# Revit family: O5DMH-NRG
name_source: partatom
category: Mechanical Equipment
revit_build: Autodesk Revit 2017 (Build: 20181011_1645(x64)
units: mm (PartAtom-declared; Revit-internal decimal feet)

## family parameters
Always vertical = Yes
Cut with Voids When Loaded = No
OmniClass Number = 23.40.40.11.17
OmniClass Title = Refrigerated Cases
Part Type = Normal
Room Calculation Point = No
Round Connector Dimension = Use Radius
Shared = No
Work Plane-Based = Yes

## types (36) — shared parameters
24" Shelf = Yes
BOTTOM ELECTRICAL = Yes
BOTTOM REFRIGERATION PIPING = Yes
Certifications = NSF 7, UL471, CSA
DATE = 05/02/2016
DRAIN PIPING = Yes
Default Elevation = 48"
Description = Multi-Deck Merchandiser
Discharge Air Velocity (FPM) = 150 FPM
EQUIPMENT DESCRIPTION = Multi-Deck Merchandiser
EQUIPMENT MARK = O5DMHQA-NRG
GLASS = Glass
Height = 85 5/8"
Item Description = Multi-Deck Merchandiser
LF STD END = Yes
Legend Number = O5DMHQA-NRG
Manufacturer = HILL PHOENIX
Model = O5DMHQA-NRG
PAINTED METAL UPPER SHELF = PAINTED SHELVES
REAR REFRIGERATION PIPING = Yes
REFRIGERATION PIPING = COPPER PIPE
RT STD END = Yes
STAINLESS STEEL = GALVANIZED STEEL
Standard Power Amps = 0 A
Superheat Set Point @ Bulb (°F) = 6-8 °F
TOP ELECTRICAL = Yes
TOP REFRIGERATION PIPING = Yes
Timed-Off Defrost Termination Temp = 42 °F
URL = http://www.hillphoenix.com
Width = 43 1/4"

## per-type parameters (varying)
| type | Application Discipline | BTUH Conventional | BTUH Parallel | CENTER LINE | DRAIN LINE | Defrosts Per Day | Discharge Air (°F) | Evaporator (°F) | High Efficiency Amps | High Efficiency Watts | High Power (Cornice) Amps | High Power (Cornice) Watts | Length | Length of Cases | Light Length | Lights Per Row | Number of Fans | Refgn | Standard Power Watts | Timed-Off Defrost Fail-Safe (Min) |
| 04' Dairy/Deli/Cut Produce with Std. Dairy Sill | Dairy/Deli/Cut Produce with 2.5 Extended Sill | 1531 | 1340 | 24" | 36" | 6 | 33 °F | 28 °F | 0 A | 18 W | 0 A | 22 W | 48" | 48" | 4' | 1 | 1 | 22 1/2" | 12 W | 40 (min) |
| 06' Dairy/Deli/Cut Produce with Std. Dairy Sill | Dairy/Deli/Cut Produce with Std. Dairy Sill | 1571 | 1375 | 36" | 36" | 6 | 33 °F | 28 °F | 0 A | 35 W | 0 A | 30 W | 72" | 72" | 3' | 2 | 2 | 28 5/8" | 17 W | 40 (min) |
| 08' Dairy/Deli/Cut Produce with Std. Dairy Sill | Dairy/Deli/Cut Produce with Std. Dairy Sill | 1571 | 1375 | 48" | 48" | 6 | 33 °F | 28 °F | 0 A | 35 W | 0 A | 43 W | 96" | 96" | 4' | 2 | 2 | 28 5/8" | 24 W | 40 (min) |
| 12' Dairy/Deli/Cut Produce with Std. Dairy Sill | Dairy/Deli/Cut Produce with Std. Dairy Sill | 1571 | 1375 | 72" | 72" | 6 | 33 °F | 28 °F | 1 A | 53 W | 1 A | 65 W | 144" | 144" | 4' | 3 | 3 | 28 5/8" | 36 W | 40 (min) |
| 04' Dairy/Deli/Cut Produce with 2.5 Extended Sill | Dairy/Deli/Cut Produce with 2.5 Extended Sill | 1531 | 1340 | 24" | 36" | 6 | 33 °F | 28 °F | 0 A | 18 W | 0 A | 22 W | 48" | 48" | 4' | 1 | 1 | 22 1/2" | 12 W | 40 (min) |
| 06' Dairy/Deli/Cut Produce with 2.5 Extended Sill | Dairy/Deli/Cut Produce with 2.5 Extended Sill | 1531 | 1340 | 36" | 36" | 6 | 33 °F | 28 °F | 0 A | 35 W | 0 A | 30 W | 72" | 72" | 3' | 2 | 2 | 28 5/8" | 17 W | 40 (min) |
| 08' Dairy/Deli/Cut Produce with 2.5 Extended Sill | Dairy/Deli/Cut Produce with 2.5 Extended Sill | 1531 | 1340 | 48" | 48" | 6 | 33 °F | 28 °F | 0 A | 35 W | 0 A | 43 W | 96" | 96" | 4' | 2 | 2 | 28 5/8" | 24 W | 40 (min) |
| 12' Dairy/Deli/Cut Produce with 2.5 Extended Sill | Dairy/Deli/Cut Produce with 2.5 Extended Sill | 1531 | 1340 | 72" | 72" | 6 | 33 °F | 28 °F | 1 A | 53 W | 1 A | 65 W | 144" | 144" | 4' | 3 | 3 | 28 5/8" | 36 W | 40 (min) |
| 04' Dairy/Deli/Cut Produce with 5 Extended Sill | Dairy/Deli/Cut Produce with 5 Extended Sill | 1503 | 1315 | 24" | 36" | 6 | 33 °F | 28 °F | 0 A | 18 W | 0 A | 22 W | 48" | 48" | 4' | 1 | 1 | 22 1/2" | 12 W | 40 (min) |
| 06' Dairy/Deli/Cut Produce with 5 Extended Sill | Dairy/Deli/Cut Produce with 5 Extended Sill | 1503 | 1315 | 36" | 36" | 6 | 33 °F | 28 °F | 0 A | 35 W | 0 A | 30 W | 72" | 72" | 3' | 2 | 2 | 28 5/8" | 17 W | 40 (min) |
| 08' Dairy/Deli/Cut Produce with 5 Extended Sill | Dairy/Deli/Cut Produce with 5 Extended Sill | 1503 | 1315 | 48" | 48" | 6 | 33 °F | 28 °F | 0 A | 35 W | 0 A | 43 W | 96" | 96" | 4' | 2 | 2 | 28 5/8" | 24 W | 40 (min) |
| 12' Dairy/Deli/Cut Produce with 5 Extended Sill | Dairy/Deli/Cut Produce with 5 Extended Sill | 1503 | 1315 | 72" | 72" | 6 | 33 °F | 28 °F | 1 A | 53 W | 1 A | 65 W | 144" | 144" | 4' | 3 | 3 | 28 5/8" | 36 W | 40 (min) |
| 04' Dairy/Deli/Cut Produce with 7.5 Extended Sill | Dairy/Deli/Cut Produce with 7.5 Extended Sill | 1480 | 1295 | 24" | 36" | 6 | 33 °F | 28 °F | 0 A | 18 W | 0 A | 22 W | 48" | 48" | 4' | 1 | 1 | 22 1/2" | 12 W | 40 (min) |
| 06' Dairy/Deli/Cut Produce with 7.5 Extended Sill | Dairy/Deli/Cut Produce with 7.5 Extended Sill | 1480 | 1295 | 36" | 36" | 6 | 33 °F | 28 °F | 0 A | 35 W | 0 A | 30 W | 72" | 72" | 3' | 2 | 2 | 28 5/8" | 17 W | 40 (min) |
| 08' Dairy/Deli/Cut Produce with 7.5 Extended Sill | Dairy/Deli/Cut Produce with 7.5 Extended Sill | 1480 | 1295 | 48" | 48" | 6 | 33 °F | 28 °F | 0 A | 35 W | 0 A | 43 W | 96" | 96" | 4' | 2 | 2 | 28 5/8" | 24 W | 40 (min) |
| 12' Dairy/Deli/Cut Produce with 7.5 Extended Sill | Dairy/Deli/Cut Produce with 7.5 Extended Sill | 1480 | 1295 | 72" | 72" | 6 | 33 °F | 28 °F | 1 A | 53 W | 1 A | 65 W | 144" | 144" | 4' | 3 | 3 | 28 5/8" | 36 W | 40 (min) |
| 04' Beverage Bulk Produce with 2.5 Extended Sill | Beverage/ Bulk Produce with 2.5 Extended Sill | 1291 | 1130 | 24" | 36" | 2 | 37 °F | 34 °F | 0 A | 18 W | 0 A | 22 W | 48" | 48" | 4' | 1 | 1 | 22 1/2" | 12 W | 30 (min) |
| 06' Beverage Bulk Produce with 2.5 Extended Sill | Beverage/ Bulk Produce with 2.5 Extended Sill | 1291 | 1130 | 36" | 36" | 2 | 37 °F | 34 °F | 0 A | 35 W | 0 A | 30 W | 72" | 72" | 3' | 2 | 2 | 28 5/8" | 17 W | 30 (min) |
| 08' Beverage Bulk Produce with 2.5 Extended Sill | Beverage/ Bulk Produce | 1291 | 1130 | 48" | 48" | 2 | 37 °F | 34 °F | 0 A | 35 W | 0 A | 43 W | 96" | 96" | 4' | 2 | 2 | 28 5/8" | 24 W | 30 (min) |
| 12' Beverage Bulk Produce with 2.5 Extended Sill | Beverage/ Bulk Produce with 2.5 Extended Sill | 1291 | 1130 | 72" | 72" | 2 | 37 °F | 34 °F | 1 A | 53 W | 1 A | 65 W | 144" | 144" | 4' | 3 | 3 | 28 5/8" | 36 W | 30 (min) |
| 04' Beverage Bulk Produce with 5 Extended Sill | Beverage/ Bulk Produce with 5 Extended Sill | 1263 | 1130 | 24" | 36" | 2 | 37 °F | 34 °F | 0 A | 18 W | 0 A | 22 W | 48" | 48" | 4' | 1 | 1 | 22 1/2" | 12 W | 30 (min) |
| 06' Beverage Bulk Produce with 5 Extended Sill | Beverage/ Bulk Produce | 1263 | 1105 | 36" | 36" | 2 | 37 °F | 34 °F | 0 A | 35 W | 0 A | 30 W | 72" | 72" | 3' | 2 | 2 | 28 5/8" | 17 W | 30 (min) |
| 08' Beverage Bulk Produce with 5 Extended Sill | Beverage/ Bulk Produce with 5 Extended Sill | 1263 | 1130 | 48" | 48" | 2 | 37 °F | 34 °F | 0 A | 35 W | 0 A | 43 W | 96" | 96" | 4' | 2 | 2 | 28 5/8" | 24 W | 30 (min) |
| 12' Beverage Bulk Produce with 5 Extended Sill | Beverage/ Bulk Produce with 5 Extended Sill | 1263 | 1105 | 72" | 72" | 2 | 37 °F | 34 °F | 1 A | 53 W | 1 A | 65 W | 144" | 144" | 4' | 3 | 3 | 28 5/8" | 36 W | 30 (min) |
| 04' Beverage Bulk Produce with 7.5 Extended Sill | Beverage/ Bulk Produce | 1240 | 1085 | 24" | 36" | 2 | 37 °F | 34 °F | 0 A | 18 W | 0 A | 22 W | 48" | 48" | 4' | 1 | 1 | 22 1/2" | 12 W | 30 (min) |
| 06' Beverage Bulk Produce with 7.5 Extended Sill | Beverage/ Bulk Produce with 7.5 Extended Sill | 1240 | 1085 | 36" | 36" | 2 | 37 °F | 34 °F | 0 A | 35 W | 0 A | 30 W | 72" | 72" | 3' | 2 | 2 | 28 5/8" | 17 W | 30 (min) |
| 08' Beverage Bulk Produce with 7.5 Extended Sill | Beverage/ Bulk Produce with 7.5 Extended Sill | 1240 | 1085 | 48" | 48" | 6 | 33 °F | 28 °F | 0 A | 35 W | 0 A | 43 W | 96" | 96" | 4' | 2 | 2 | 28 5/8" | 24 W | 40 (min) |
| 12' Beverage Bulk Produce with 7.5 Extended Sill | Beverage/ Bulk Produce with 7.5 Extended Sill | 1240 | 1085 | 72" | 72" | 2 | 37 °F | 34 °F | 1 A | 53 W | 1 A | 65 W | 144" | 144" | 4' | 3 | 3 | 28 5/8" | 36 W | 30 (min) |
| 04' Beverage Bulk Produce with Std. Dairy Sill | Beverage Bulk Produce with Std. Dairy Sill | 1331 | 1165 | 24" | 36" | 2 | 37 °F | 34 °F | 0 A | 18 W | 0 A | 22 W | 48" | 48" | 4' | 1 | 1 | 22 1/2" | 12 W | 30 (min) |
| 06' Beverage Bulk Produce with Std. Dairy Sill | Beverage/ Bulk Produce with 2.5 Extended Sill | 1331 | 1165 | 36" | 36" | 2 | 37 °F | 34 °F | 0 A | 35 W | 0 A | 30 W | 72" | 72" | 3' | 2 | 2 | 28 5/8" | 17 W | 30 (min) |
| 08' Beverage Bulk Produce with Std. Dairy Sill | Beverage/ Bulk Produce with 2.5 Extended Sill | 1331 | 1164 | 48" | 48" | 2 | 37 °F | 34 °F | 0 A | 35 W | 0 A | 43 W | 96" | 96" | 4' | 2 | 2 | 28 5/8" | 24 W | 30 (min) |
| 12' Beverage Bulk Produce with Std. Dairy Sill | Beverage/ Bulk Produce | 1331 | 1165 | 72" | 72" | 2 | 37 °F | 34 °F | 1 A | 53 W | 1 A | 65 W | 144" | 144" | 4' | 3 | 3 | 28 5/8" | 36 W | 30 (min) |
| 12' | Dairy/Deli/Cut Produce | 1480 | 1295 | 72" | 72" | 2 | 33 °F | 28 °F | 1 A | 53 W | 0 A | 45 W | 144" | 48" | 4' | 3 | 3 | 28 5/8" | 18 W | 30 (min) |
| 8' | Dairy/Deli/Cut Produce | 1503 | 1315 | 48" | 48" | 2 | 33 °F | 28 °F | 0 A | 35 W | 0 A | 30 W | 96" | 48" | 4' | 2 | 2 | 28 5/8" | 12 W | 30 (min) |
| 6' | Dairy/Deli/Cut Produce | 1531 | 1340 | 36" | 36" | 2 | 33 °F | 28 °F | 0 A | 35 W | 0 A | 24 W | 72" | 48" | 3 | 2 | 2 | 28 5/8" | 9 W | 30 (min) |
| 4' | Dairy/Deli/Cut Produce | 1571 | 1375 | 24" | 36" | 6 | 33 °F | 28 °F | 0 A | 18 W | 0 A | 15 W | 48" | 48" | 4' | 1 | 1 | 22 1/2" | 6 W | 40 (Min) |

## geometry (parser evidence)
native form markers: Blend x15, Sweep x9
no freeform markers — native parametric forms only
